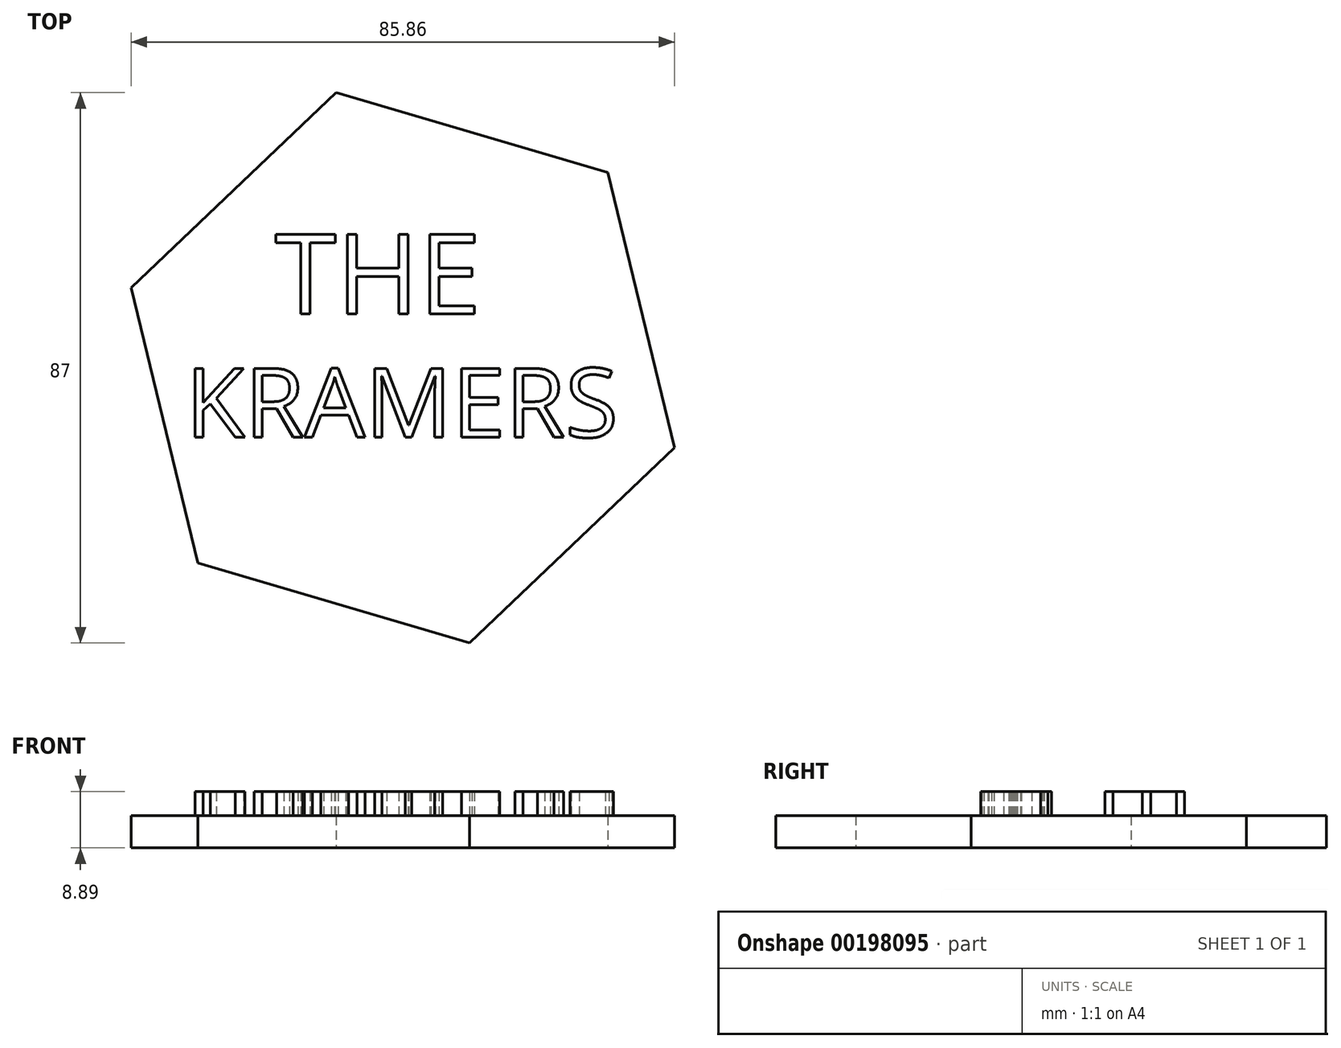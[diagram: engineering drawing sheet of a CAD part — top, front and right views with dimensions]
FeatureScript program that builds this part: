
annotation { "Feature Type Name" : "Feature", "Feature Type Description" : "" }
export const myFeature = defineFeature(function(context is Context, id is Id, definition is map)
    precondition{}
    {
        {
            var Q0;
            Q0=qCreatedBy(makeId("Top.planeOp"),FACE);
            var sketch = newSketch(context, id + "F0", { "sketchPlane" : qUnion([Q0])});
            skCircle(sketch, "E0.cCircle", {"center": v(0, 0) * mm, "radius": 38.76 * mm, "construction": true});
            skLineSegment(sketch, "E0.0", {"start": v(-32.41, -30.86) * mm, "end": v(-42.93, 12.64) * mm});
            skLineSegment(sketch, "E0.1", {"start": v(-42.93, 12.64) * mm, "end": v(-10.52, 43.5) * mm});
            skLineSegment(sketch, "E0.2", {"start": v(-10.52, 43.5) * mm, "end": v(32.41, 30.86) * mm});
            skLineSegment(sketch, "E0.3", {"start": v(32.41, 30.86) * mm, "end": v(42.93, -12.64) * mm});
            skLineSegment(sketch, "E0.4", {"start": v(42.93, -12.64) * mm, "end": v(10.52, -43.5) * mm});
            skLineSegment(sketch, "E0.5", {"start": v(10.52, -43.5) * mm, "end": v(-32.41, -30.86) * mm});
            skPoint(sketch, "E0.0.midPoint", {"position": v(-37.67, -9.11) * mm});
            skSolve(sketch);
        }
        {
            var Q0;
            Q0 = qSketchRegion(id + "F0", true);
            extrude(context, id + "F1", {"entities" : qUnion([Q0]), "depth" : 5.08 * mm});
        }
        {
            var Q0;
            Q0=makeQuery(id+"F1.opExtrude","CAP_FACE",FACE,{"disambiguationData":[OSD([sQuery(id+"F0.wireOp",EDGE,"E0.0"),sQuery(id+"F0.wireOp",EDGE,"E0.1"),sQuery(id+"F0.wireOp",EDGE,"E0.2"),sQuery(id+"F0.wireOp",EDGE,"E0.3"),sQuery(id+"F0.wireOp",EDGE,"E0.4"),sQuery(id+"F0.wireOp",EDGE,"E0.5")])],"isStart":false});
            var sketch = newSketch(context, id + "F2", { "sketchPlane" : qUnion([Q0])});
            skText(sketch, "E1", { "text": "THE", "fontName": "OpenSans-Regular.ttf"});
            skText(sketch, "E2", { "text": "KRAMERS", "fontName": "OpenSans-Regular.ttf"});
            const initialGuessF2  = {"E1": [-0.02024, 0.0085, 1, 0, 0.0127], "E2": [-0.0343, -0.01095, 1, 0, 0.01095]};
            skSetInitialGuess(sketch, initialGuessF2);
            skSolve(sketch);
        }
        {
            var Q0;
            Q0 = qSketchRegion(id + "F2", true);
            extrude(context, id + "F3", {"entities" : qUnion([Q0]), "operationType" : NewBodyOperationType.ADD, "depth" : 3.8 * mm});
        }
    });
